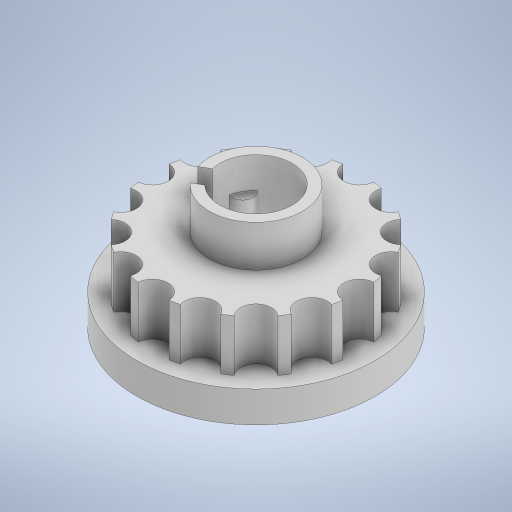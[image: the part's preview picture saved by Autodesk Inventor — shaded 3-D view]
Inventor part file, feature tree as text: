
AUTODESK INVENTOR PART (.ipt)
format: ipt  version: 2023 (Build 270158000, 158)  size: 380,928 bytes
history: native  units: mm
features: extrude x6, sketch x6, other x1
ambient origin geometry x8: Origin, YZ Plane, XZ Plane, XY Plane, X Axis, Y Axis, Z Axis, Center Point
bodies: Body1 (feature_tree)
feature tree (13):
  other  "Твердое тело1"
  extrude  "Выдавливание1"  Depth=23.0mm
  extrude  "Выдавливание2"  Depth=17.0mm
  extrude  "Выдавливание3"  Depth=3.0mm TaperAngle=0.0deg
  extrude  "Выдавливание4"  Depth=20.0mm
  extrude  "Выдавливание5"  Depth=3.0mm
  extrude  "Выдавливание6"  Depth=160.0mm TaperAngle=360.0deg
  sketch  "Эскиз1"
  sketch  "Эскиз2"
  sketch  "Эскиз3"
  sketch  "Эскиз4"
  sketch  "Эскиз5"
  sketch  "Эскиз6"
